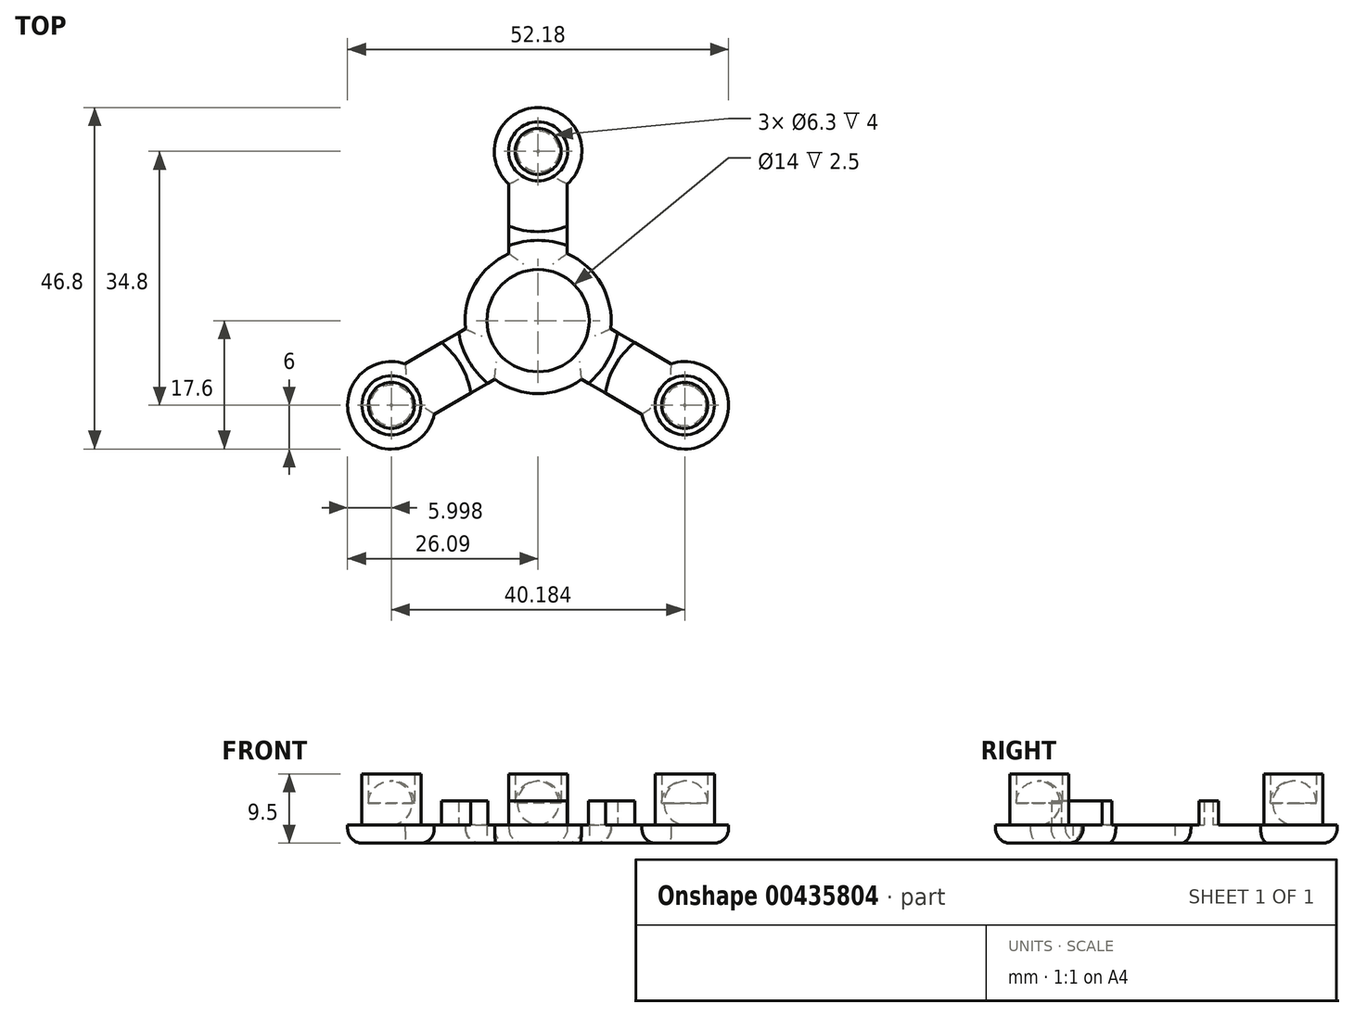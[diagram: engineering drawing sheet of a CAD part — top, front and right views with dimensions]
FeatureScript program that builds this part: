
annotation { "Feature Type Name" : "Feature", "Feature Type Description" : "" }
export const myFeature = defineFeature(function(context is Context, id is Id, definition is map)
    precondition{}
    {
        {
            var Q0;
            Q0=qCreatedBy(makeId("Top.planeOp"),FACE);
            var sketch = newSketch(context, id + "F0", { "sketchPlane" : qUnion([Q0])});
            skCircle(sketch, "E0", {"center": v(0, 0) * mm, "radius": 11.6 * mm, "construction": true});
            skCircle(sketch, "E1", {"center": v(0, 0) * mm, "radius": 7 * mm});
            skCircle(sketch, "E2", {"center": v(0, 23.2) * mm, "radius": 11.6 * mm, "construction": true});
            skCircle(sketch, "E3", {"center": v(0, 23.2) * mm, "radius": 6 * mm});
            skLineSegment(sketch, "E4", {"start": v(4, 18.73) * mm, "end": v(4, 5.74) * mm});
            skLineSegment(sketch, "E5", {"start": v(-4, 18.73) * mm, "end": v(-4, 5.74) * mm});
            skCircle(sketch, "E6.0", {"center": v(0, 0) * mm, "radius": 10 * mm});
            skLineSegment(sketch, "E7", {"start": v(0, 0) * mm, "end": v(-21.38, 12.34) * mm, "construction": true});
            skLineSegment(sketch, "E8", {"start": v(0, 0) * mm, "end": v(0, -26.62) * mm, "construction": true});
            skSolve(sketch);
        }
        {
            var Q0;
            Q0 = qSketchRegion(id + "F0", true);
            extrude(context, id + "F1", {"entities" : qUnion([Q0]), "depth" : 2.5 * mm, "offsetDistance" : 25 * mm});
        }
        {
            var Q0;
            Q0=makeQuery(id+"F1.opExtrude","CAP_FACE",FACE,{"disambiguationData":[OSD([sQuery(id+"F0.wireOp",EDGE,"E1"),sQuery(id+"F0.wireOp",EDGE,"E3"),sQuery(id+"F0.wireOp",EDGE,"E4"),sQuery(id+"F0.wireOp",EDGE,"E5"),sQuery(id+"F0.wireOp",EDGE,"E6.0")])],"isStart":false});
            var sketch = newSketch(context, id + "F2", { "sketchPlane" : qUnion([Q0])});
            skCircle(sketch, "E9", {"center": v(0, 23.2) * mm, "radius": 4.05 * mm});
            skCircle(sketch, "E10", {"center": v(0, 23.2) * mm, "radius": 3.15 * mm});
            skCircle(sketch, "E11", {"center": v(0, 0) * mm, "radius": 11 * mm});
            skCircle(sketch, "E12", {"center": v(0, 0) * mm, "radius": 11.6 * mm});
            skLineSegment(sketch, "E13", {"start": v(-4, 10.25) * mm, "end": v(-4, 10.89) * mm});
            skLineSegment(sketch, "E14", {"start": v(4, 10.25) * mm, "end": v(4, 10.89) * mm});
            skCircle(sketch, "E15", {"center": v(0, 23.2) * mm, "radius": 11.6 * mm});
            skCircle(sketch, "E16", {"center": v(0, 23.2) * mm, "radius": 11 * mm});
            skLineSegment(sketch, "E17", {"start": v(-4, 12.31) * mm, "end": v(-4, 12.95) * mm});
            skLineSegment(sketch, "E18", {"start": v(4, 12.31) * mm, "end": v(4, 12.95) * mm});
            skLineSegment(sketch, "E19", {"start": v(-4, 12.31) * mm, "end": v(-4, 10.89) * mm});
            skLineSegment(sketch, "E20", {"start": v(4, 12.31) * mm, "end": v(4, 10.89) * mm});
            skSolve(sketch);
        }
        {
            var Q0;
            Q0=makeQuery(id+"F2.imprint","IMPRINT",FACE,{"disambiguationData":[TD([[makeQuery(id+"F2.imprint","IMPRINT",EDGE,{"derivedFrom":sQuery(id+"F2.wireOp",EDGE,"E9")}),1.0]])]});
            extrude(context, id + "F3", {"entities" : qUnion([Q0]), "operationType" : NewBodyOperationType.ADD, "depth" : 7 * mm, "offsetDistance" : 25 * mm});
        }
        {
            var Q0;
            {var subQ0=sQuery(id+"F2.wireOp",EDGE,"E13");Q0=makeQuery(id+"F2.imprint","IMPRINT",FACE,{"disambiguationData":[TD([[makeQuery(id+"F2.imprint","IMPRINT",EDGE,{"derivedFrom":subQ0}),1.0]])]});}
            var Q1;
            {var subQ0=sQuery(id+"F2.wireOp",EDGE,"E17");Q1=makeQuery(id+"F2.imprint","IMPRINT",FACE,{"disambiguationData":[TD([[makeQuery(id+"F2.imprint","IMPRINT",EDGE,{"derivedFrom":subQ0}),1.0]])]});}
            var Q2;
            {var subQ0=sQuery(id+"F2.wireOp",EDGE,"E19");Q2=makeQuery(id+"F2.imprint","IMPRINT",FACE,{"disambiguationData":[TD([[makeQuery(id+"F2.imprint","IMPRINT",EDGE,{"derivedFrom":subQ0}),1.0]])]});}
            var Q3;
            {var subQ0=sQuery(id+"F2.wireOp",EDGE,"E20");Q3=makeQuery(id+"F2.imprint","IMPRINT",FACE,{"disambiguationData":[TD([[makeQuery(id+"F2.imprint","IMPRINT",EDGE,{"derivedFrom":subQ0}),-1.0]])]});}
            extrude(context, id + "F4", {"entities" : qUnion([Q0, Q1, Q2, Q3]), "operationType" : NewBodyOperationType.ADD, "depth" : 3.3 * mm, "offsetDistance" : 25 * mm});
        }
        {
            var Q0;
            Q0=makeQuery(id+"F3.opExtrude","CAP_EDGE",EDGE,{"disambiguationData":[OSD([sQuery(id+"F2.wireOp",EDGE,"E10")])],"isStart":true});
            fillet(context, id + "F5", {"entities" : qUnion([Q0]), "radius" : 3 * mm, "tangentPropagation" : true, "allowEdgeOverflow" : false});
        }
        {
            var Q0;
            Q0=makeQuery(id+"F1.opExtrude","SWEPT_BODY",BODY,{"disambiguationData":[OSD([sQuery(id+"F0.wireOp",EDGE,"E1"),sQuery(id+"F0.wireOp",EDGE,"E3"),sQuery(id+"F0.wireOp",EDGE,"E4"),sQuery(id+"F0.wireOp",EDGE,"E5"),sQuery(id+"F0.wireOp",EDGE,"E6.0")])]});
            var Q1;
            Q1=makeQuery(id+"F4.opExtrude","SWEPT_BODY",BODY,{"disambiguationData":[OSD([sQuery(id+"F2.wireOp",EDGE,"E11"),sQuery(id+"F2.wireOp",EDGE,"E12"),sQuery(id+"F2.wireOp",EDGE,"E13"),sQuery(id+"F2.wireOp",EDGE,"E14")])]});
            var Q2;
            Q2=makeQuery(id+"F4.opExtrude","SWEPT_BODY",BODY,{"disambiguationData":[OSD([sQuery(id+"F2.wireOp",EDGE,"E15"),sQuery(id+"F2.wireOp",EDGE,"E16"),sQuery(id+"F2.wireOp",EDGE,"E17"),sQuery(id+"F2.wireOp",EDGE,"E18")])]});
            var Q3;
            Q3=sQuery(id+"F0.wireOp",EDGE,"E1");
            circularPattern(context, id + "F6", {"operationType" : NewBodyOperationType.ADD, "entities" : qUnion([Q0, Q1, Q2]), "axis" : qUnion([Q3]), "angle" : 360 * degree, "instanceCount" : 3, "equalSpace" : true});
        }
        {
            var Q0;
            Q0=makeQuery(id+"F6.opPattern","COPY",EDGE,{"derivedFrom":makeQuery(id+"F1.opExtrude","CAP_EDGE",EDGE,{"disambiguationData":[OSD([sQuery(id+"F0.wireOp",EDGE,"E5")])],"isStart":true}),"instanceName":"1"});
            var Q1;
            Q1=makeQuery(id+"F6.opPattern","COPY",EDGE,{"derivedFrom":makeQuery(id+"F1.opExtrude","CAP_EDGE",EDGE,{"disambiguationData":[OSD([sQuery(id+"F0.wireOp",EDGE,"E3")])],"isStart":true}),"instanceName":"1"});
            var Q2;
            {var subQ0=sQuery(id+"F0.wireOp",EDGE,"E5");var subQ1=sQuery(id+"F0.wireOp",EDGE,"E6.0");Q2=makeQuery(id+"F6.boolean.opBoolean","SPLIT",EDGE,{"disambiguationData":[TD([makeQuery(id+"F6.opPattern","COPY",FACE,{"derivedFrom":makeQuery(id+"F4.boolean.opBoolean","MERGE",FACE,{"derivedFrom":[makeQuery(id+"F1.opExtrude","SWEPT_FACE",FACE,{"disambiguationData":[OSD([subQ0])]}),makeQuery(id+"F4.opExtrude","SWEPT_FACE",FACE,{"disambiguationData":[OSD([sQuery(id+"F2.wireOp",EDGE,"E13"),sQuery(id+"F2.wireOp",EDGE,"E17"),sQuery(id+"F2.wireOp",EDGE,"E19")])]})]}),"instanceName":"1"})])],"derivedFrom":makeQuery(id+"F1.opExtrude","CAP_EDGE",EDGE,{"disambiguationData":[OSD([subQ1])],"isStart":true})});}
            var Q3;
            Q3=makeQuery(id+"F6.opPattern","COPY",EDGE,{"derivedFrom":makeQuery(id+"F1.opExtrude","CAP_EDGE",EDGE,{"disambiguationData":[OSD([sQuery(id+"F0.wireOp",EDGE,"E4")])],"isStart":true}),"instanceName":"1"});
            var Q4;
            {var subQ0=sQuery(id+"F0.wireOp",EDGE,"E6.0");var subQ1=sQuery(id+"F0.wireOp",EDGE,"E5");Q4=makeQuery(id+"F6.boolean.opBoolean","SPLIT",EDGE,{"disambiguationData":[TD([makeQuery(id+"F1.opExtrude","SWEPT_FACE",FACE,{"disambiguationData":[OSD([subQ1])]})])],"derivedFrom":makeQuery(id+"F1.opExtrude","CAP_EDGE",EDGE,{"disambiguationData":[OSD([subQ0])],"isStart":true})});}
            var Q5;
            {var subQ0=sQuery(id+"F0.wireOp",EDGE,"E4");var subQ1=sQuery(id+"F0.wireOp",EDGE,"E6.0");Q5=makeQuery(id+"F6.boolean.opBoolean","SPLIT",EDGE,{"disambiguationData":[TD([makeQuery(id+"F1.opExtrude","SWEPT_FACE",FACE,{"disambiguationData":[OSD([subQ0])]})])],"derivedFrom":makeQuery(id+"F1.opExtrude","CAP_EDGE",EDGE,{"disambiguationData":[OSD([subQ1])],"isStart":true})});}
            var Q6;
            Q6=makeQuery(id+"F6.opPattern","COPY",EDGE,{"derivedFrom":makeQuery(id+"F1.opExtrude","CAP_EDGE",EDGE,{"disambiguationData":[OSD([sQuery(id+"F0.wireOp",EDGE,"E5")])],"isStart":true}),"instanceName":"2"});
            var Q7;
            Q7=makeQuery(id+"F6.opPattern","COPY",EDGE,{"derivedFrom":makeQuery(id+"F1.opExtrude","CAP_EDGE",EDGE,{"disambiguationData":[OSD([sQuery(id+"F0.wireOp",EDGE,"E3")])],"isStart":true}),"instanceName":"2"});
            var Q8;
            Q8=makeQuery(id+"F6.opPattern","COPY",EDGE,{"derivedFrom":makeQuery(id+"F1.opExtrude","CAP_EDGE",EDGE,{"disambiguationData":[OSD([sQuery(id+"F0.wireOp",EDGE,"E4")])],"isStart":true}),"instanceName":"2"});
            var Q9;
            Q9=makeQuery(id+"F1.opExtrude","CAP_EDGE",EDGE,{"disambiguationData":[OSD([sQuery(id+"F0.wireOp",EDGE,"E4")])],"isStart":true});
            var Q10;
            Q10=makeQuery(id+"F1.opExtrude","CAP_EDGE",EDGE,{"disambiguationData":[OSD([sQuery(id+"F0.wireOp",EDGE,"E3")])],"isStart":true});
            var Q11;
            Q11=makeQuery(id+"F1.opExtrude","CAP_EDGE",EDGE,{"disambiguationData":[OSD([sQuery(id+"F0.wireOp",EDGE,"E5")])],"isStart":true});
            fillet(context, id + "F7", {"entities" : qUnion([Q0, Q1, Q2, Q3, Q4, Q5, Q6, Q7, Q8, Q9, Q10, Q11]), "radius" : 2 * mm, "tangentPropagation" : true, "allowEdgeOverflow" : false});
        }
    });
